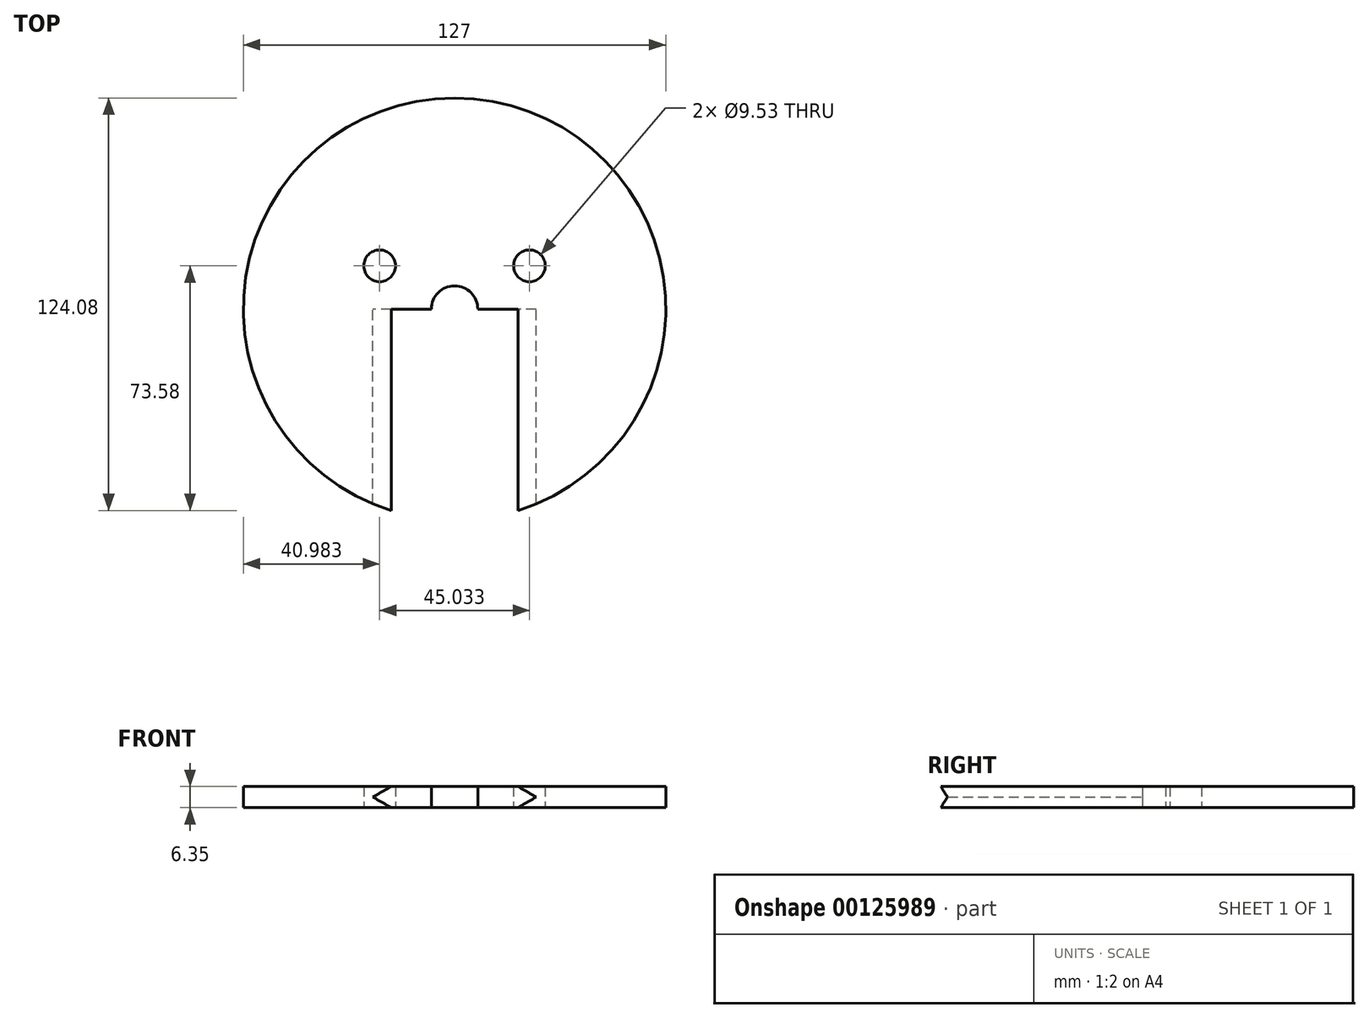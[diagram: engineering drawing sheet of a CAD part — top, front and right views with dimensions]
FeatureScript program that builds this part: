
annotation { "Feature Type Name" : "Feature", "Feature Type Description" : "" }
export const myFeature = defineFeature(function(context is Context, id is Id, definition is map)
    precondition{}
    {
        {
            var Q0;
            Q0=qCreatedBy(makeId("Top.planeOp"),FACE);
            var sketch = newSketch(context, id + "F0", { "sketchPlane" : qUnion([Q0])});
            skCircle(sketch, "E0", {"center": v(0, 0) * mm, "radius": 63.5 * mm});
            skCircle(sketch, "E1", {"center": v(0, 0) * mm, "radius": 7 * mm});
            skLineSegment(sketch, "E2.bottom", {"start": v(-19.05, 0) * mm, "end": v(19.05, 0) * mm});
            skLineSegment(sketch, "E2.top", {"start": v(-19.05, -72.34) * mm, "end": v(19.05, -72.34) * mm});
            skLineSegment(sketch, "E2.left", {"start": v(-19.05, 0) * mm, "end": v(-19.05, -72.34) * mm});
            skLineSegment(sketch, "E2.right", {"start": v(19.05, 0) * mm, "end": v(19.05, -72.34) * mm});
            skSolve(sketch);
        }
        {
            var Q0;
            {var subQ5=sQuery(id+"F0.wireOp",EDGE,"E2.left");var subQ8=sQuery(id+"F0.wireOp",EDGE,"E0");var subQ9=makeQuery(id+"F0.imprint","INTERSECT",VERTEX,{"derivedFrom":[subQ8,subQ5]});Q0=makeQuery(id+"F0.imprint","IMPRINT",FACE,{"disambiguationData":[TD([[makeQuery(id+"F0.imprint","IMPRINT",EDGE,{"disambiguationData":[TD([[subQ9,1.0]])],"derivedFrom":subQ8}),1.0]])]});}
            extrude(context, id + "F1", {"entities" : qUnion([Q0]), "depth" : 6.35 * mm});
        }
        {
            var Q0;
            {var subQ0=sQuery(id+"F0.wireOp",EDGE,"E2.bottom");Q0=makeQuery(id+"F1.opExtrude","SWEPT_FACE",FACE,{"disambiguationData":[OSD([subQ0]),TDD([makeQuery(id+"F0.imprint","IMPRINT",EDGE,{"disambiguationData":[TD([[makeQuery(id+"F0.imprint","INTERSECT",VERTEX,{"derivedFrom":[subQ0,sQuery(id+"F0.wireOp",EDGE,"E2.right")]}),1.0]])],"derivedFrom":subQ0})])]});}
            var sketch = newSketch(context, id + "F2", { "sketchPlane" : qUnion([Q0])});
            skLineSegment(sketch, "E3", {"start": v(19.05, 6.35) * mm, "end": v(24.55, 3.18) * mm});
            skLineSegment(sketch, "E4", {"start": v(24.55, 3.18) * mm, "end": v(19.05, 0) * mm});
            skSolve(sketch);
        }
        {
            var Q0;
            {var subQ0=sQuery(id+"F0.wireOp",EDGE,"E2.bottom");Q0=makeQuery(id+"F1.opExtrude","SWEPT_FACE",FACE,{"disambiguationData":[OSD([subQ0]),TDD([makeQuery(id+"F0.imprint","IMPRINT",EDGE,{"disambiguationData":[TD([[makeQuery(id+"F0.imprint","INTERSECT",VERTEX,{"derivedFrom":[subQ0,sQuery(id+"F0.wireOp",EDGE,"E2.left")]}),-1.0]])],"derivedFrom":subQ0})])]});}
            var sketch = newSketch(context, id + "F3", { "sketchPlane" : qUnion([Q0])});
            skLineSegment(sketch, "E5", {"start": v(-19.05, 6.35) * mm, "end": v(-24.55, 3.18) * mm});
            skLineSegment(sketch, "E6", {"start": v(-24.55, 3.17) * mm, "end": v(-19.05, 0) * mm});
            skSolve(sketch);
        }
        {
            var Q0;
            Q0=makeQuery(id+"F2.imprint","IMPRINT",FACE,{"disambiguationData":[TD([[makeQuery(id+"F2.imprint","IMPRINT",EDGE,{"derivedFrom":sQuery(id+"F2.wireOp",EDGE,"E3")}),-1.0]])]});
            var Q1;
            Q1=makeQuery(id+"F3.imprint","IMPRINT",FACE,{"disambiguationData":[TD([[makeQuery(id+"F3.imprint","IMPRINT",EDGE,{"derivedFrom":sQuery(id+"F3.wireOp",EDGE,"E5")}),1.0]])]});
            extrude(context, id + "F4", {"entities" : qUnion([Q0, Q1]), "operationType" : NewBodyOperationType.REMOVE, "depth" : 69.85 * mm});
        }
        {
            var Q0;
            Q0=makeQuery(id+"F1.opExtrude","CAP_FACE",FACE,{"disambiguationData":[OSD([sQuery(id+"F0.wireOp",EDGE,"E0"),sQuery(id+"F0.wireOp",EDGE,"E1"),sQuery(id+"F0.wireOp",EDGE,"E2.bottom"),sQuery(id+"F0.wireOp",EDGE,"E2.left"),sQuery(id+"F0.wireOp",EDGE,"E2.right")])],"isStart":false});
            var sketch = newSketch(context, id + "F5", { "sketchPlane" : qUnion([Q0]), "disableImprinting" : false});
            skPoint(sketch, "E7", {"position": v(0, 0) * mm});
            skPoint(sketch, "E8", {"position": v(-22.52, 13) * mm});
            skPoint(sketch, "E9", {"position": v(22.52, 13) * mm});
            skLineSegment(sketch, "E10", {"start": v(-22.52, 13) * mm, "end": v(0, 0) * mm});
            skLineSegment(sketch, "E11", {"start": v(0, 0) * mm, "end": v(22.52, 13) * mm});
            skLineSegment(sketch, "E12", {"start": v(0, 0) * mm, "end": v(0, -48.95) * mm});
            skCircle(sketch, "E13", {"center": v(0, 0) * mm, "radius": 20 * mm});
            skSolve(sketch);
        }
        {
            var Q0;
            Q0=sQuery(id+"F5.wireOp",VERTEX,"E8");
            var Q1;
            Q1=sQuery(id+"F5.wireOp",VERTEX,"E9");
            var Q2;
            Q2=makeQuery(id+"F1.opExtrude","SWEPT_BODY",BODY,{"disambiguationData":[OSD([sQuery(id+"F0.wireOp",EDGE,"E0"),sQuery(id+"F0.wireOp",EDGE,"E1"),sQuery(id+"F0.wireOp",EDGE,"E2.bottom"),sQuery(id+"F0.wireOp",EDGE,"E2.left"),sQuery(id+"F0.wireOp",EDGE,"E2.right")])]});
            hole(context, id + "F6", {"style" : HoleStyle.SIMPLE, "endStyle" : HoleEndStyle.BLIND, "holeDiameter" : 9.53 * mm, "majorDiameter" : 5 * mm, "holeDepth" : 10 * mm, "locations" : qUnion([Q0, Q1]), "scope" : qUnion([Q2]), "tappedDepth" : 12 * mm, "tapClearance" : 3});
        }
    });
